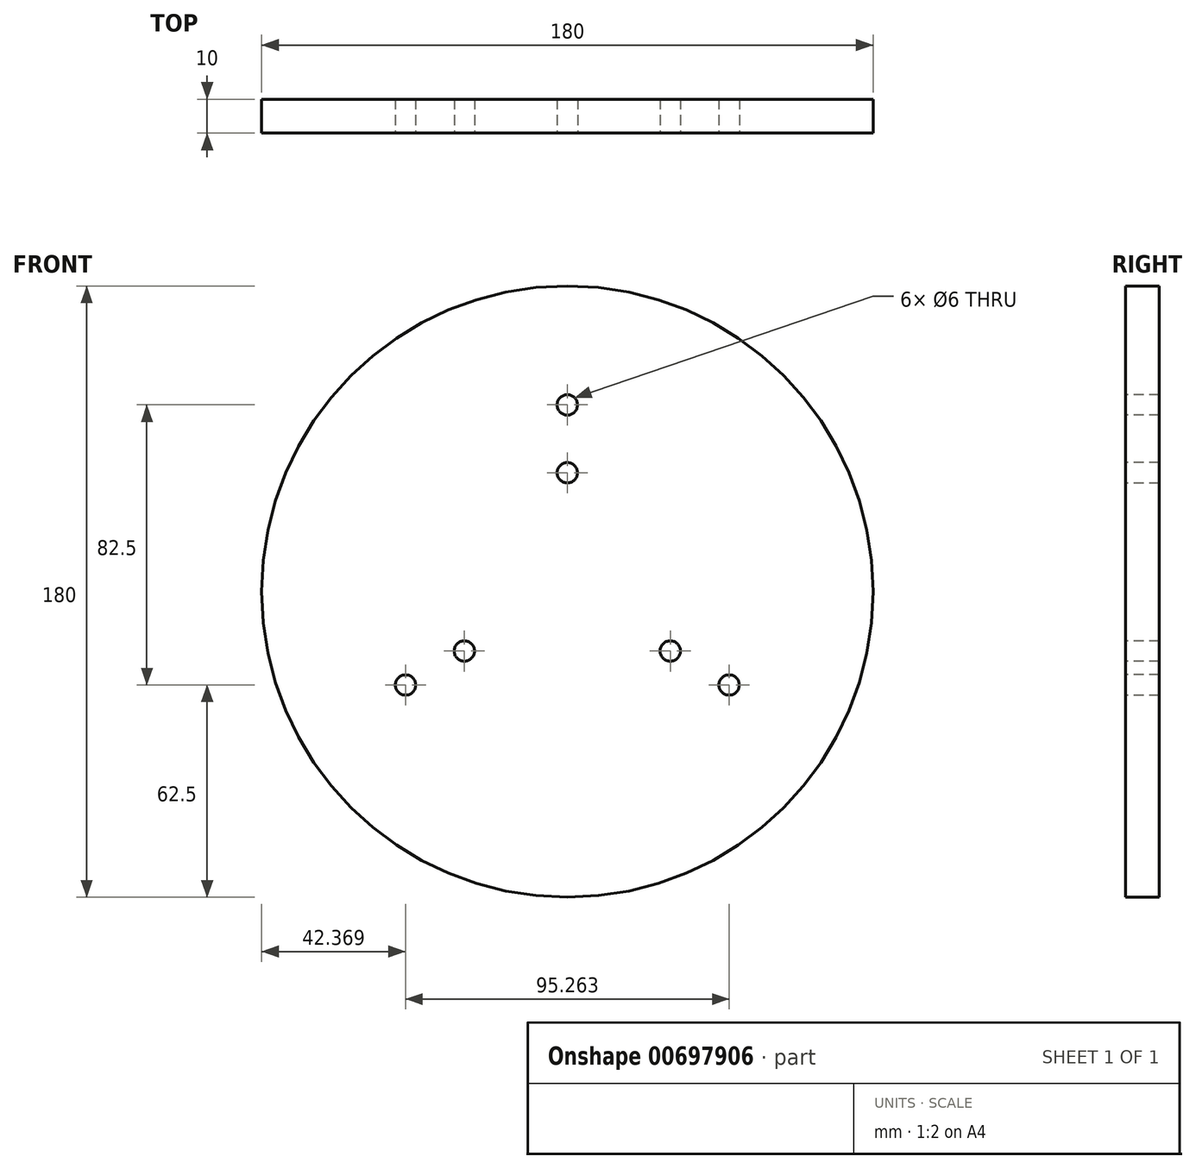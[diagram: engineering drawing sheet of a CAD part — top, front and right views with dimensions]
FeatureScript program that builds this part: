
annotation { "Feature Type Name" : "Feature", "Feature Type Description" : "" }
export const myFeature = defineFeature(function(context is Context, id is Id, definition is map)
    precondition{}
    {
        {
            var Q0;
            Q0=qCreatedBy(makeId("Front.planeOp"),FACE);
            var sketch = newSketch(context, id + "F0", { "sketchPlane" : qUnion([Q0])});
            skLineSegment(sketch, "E0.bottom", {"start": v(90, -90) * mm, "end": v(-90, -90) * mm});
            skLineSegment(sketch, "E0.top", {"start": v(90, 90) * mm, "end": v(-90, 90) * mm});
            skLineSegment(sketch, "E0.left", {"start": v(90, -90) * mm, "end": v(90, 90) * mm});
            skLineSegment(sketch, "E0.right", {"start": v(-90, -90) * mm, "end": v(-90, 90) * mm});
            skPoint(sketch, "E0.middle", {"position": v(0, 0) * mm});
            skSolve(sketch);
        }
        {
            var Q0;
            Q0=qSketchRegion(id+"F0",true);
            extrude(context, id + "F1", {"entities" : qUnion([Q0]), "oppositeDirection" : true, "depth" : 10 * mm, "offsetDistance" : 25 * mm});
        }
        {
            var Q0;
            Q0=makeQuery(id+"F0.imprint","IMPRINT",FACE,{"disambiguationData":[TD([[makeQuery(id+"F0.imprint","IMPRINT",EDGE,{"derivedFrom":sQuery(id+"F0.wireOp",EDGE,"E0.bottom")}),-1.0]])]});
            var sketch = newSketch(context, id + "F2", { "sketchPlane" : qUnion([Q0])});
            skPoint(sketch, "E1.middle", {"position": v(0, 0) * mm});
            skLineSegment(sketch, "E2", {"start": v(0, 90) * mm, "end": v(0, 0) * mm, "construction": true});
            skCircle(sketch, "E3", {"center": v(0, 55) * mm, "radius": 3 * mm});
            skCircle(sketch, "E4", {"center": v(0, 35) * mm, "radius": 3 * mm});
            skLineSegment(sketch, "E5.1.0", {"start": v(-77.94, -45) * mm, "end": v(0, 0) * mm, "construction": true});
            skCircle(sketch, "E5.1.1", {"center": v(-30.31, -17.5) * mm, "radius": 3 * mm});
            skCircle(sketch, "E5.1.2", {"center": v(-47.63, -27.5) * mm, "radius": 3 * mm});
            skLineSegment(sketch, "E5.2.0", {"start": v(77.94, -45) * mm, "end": v(0, 0) * mm, "construction": true});
            skCircle(sketch, "E5.2.1", {"center": v(30.31, -17.5) * mm, "radius": 3 * mm});
            skCircle(sketch, "E5.2.2", {"center": v(47.63, -27.5) * mm, "radius": 3 * mm});
            skSolve(sketch);
        }
        {
            var Q0;
            Q0=qSketchRegion(id+"F2",true);
            extrude(context, id + "F3", {"entities" : qUnion([Q0]), "operationType" : NewBodyOperationType.REMOVE, "endBound" : BoundingType.THROUGH_ALL, "oppositeDirection" : true, "depth" : 1 * mm, "offsetDistance" : 25 * mm});
        }
        {
            var Q0;
            Q0=makeQuery(id+"F0.imprint","IMPRINT",FACE,{"disambiguationData":[TD([[makeQuery(id+"F0.imprint","IMPRINT",EDGE,{"derivedFrom":sQuery(id+"F0.wireOp",EDGE,"E0.bottom")}),-1.0]])]});
            var sketch = newSketch(context, id + "F4", { "sketchPlane" : qUnion([Q0])});
            skCircle(sketch, "E6", {"center": v(0, 0) * mm, "radius": 90 * mm});
            skSolve(sketch);
        }
        {
            var Q0;
            {var subQ0=sQuery(id+"F4.wireOp",EDGE,"E6");var subQ1=makeQuery(id+"F0.imprint","IMPRINT",EDGE,{"derivedFrom":sQuery(id+"F0.wireOp",EDGE,"E0.top")});var subQ2=makeQuery(id+"F4.imprint","INTERSECT",VERTEX,{"derivedFrom":[subQ1,subQ0]});Q0=makeQuery(id+"F4.imprint","IMPRINT",FACE,{"disambiguationData":[TD([[makeQuery(id+"F4.imprint","IMPRINT",EDGE,{"disambiguationData":[TD([[subQ2,-1.0]])],"derivedFrom":subQ0}),-1.0]])]});}
            var Q1;
            {var subQ0=sQuery(id+"F4.wireOp",EDGE,"E6");var subQ1=makeQuery(id+"F0.imprint","IMPRINT",EDGE,{"derivedFrom":sQuery(id+"F0.wireOp",EDGE,"E0.top")});var subQ2=makeQuery(id+"F4.imprint","INTERSECT",VERTEX,{"derivedFrom":[subQ1,subQ0]});Q1=makeQuery(id+"F4.imprint","IMPRINT",FACE,{"disambiguationData":[TD([[makeQuery(id+"F4.imprint","IMPRINT",EDGE,{"disambiguationData":[TD([[subQ2,1.0]])],"derivedFrom":subQ0}),-1.0]])]});}
            var Q2;
            {var subQ0=sQuery(id+"F4.wireOp",EDGE,"E6");var subQ1=makeQuery(id+"F0.imprint","IMPRINT",EDGE,{"derivedFrom":sQuery(id+"F0.wireOp",EDGE,"E0.left")});var subQ2=makeQuery(id+"F4.imprint","INTERSECT",VERTEX,{"derivedFrom":[subQ1,subQ0]});Q2=makeQuery(id+"F4.imprint","IMPRINT",FACE,{"disambiguationData":[TD([[makeQuery(id+"F4.imprint","IMPRINT",EDGE,{"disambiguationData":[TD([[subQ2,1.0]])],"derivedFrom":subQ0}),-1.0]])]});}
            var Q3;
            {var subQ0=sQuery(id+"F4.wireOp",EDGE,"E6");var subQ1=makeQuery(id+"F0.imprint","IMPRINT",EDGE,{"derivedFrom":sQuery(id+"F0.wireOp",EDGE,"E0.right")});var subQ2=makeQuery(id+"F4.imprint","INTERSECT",VERTEX,{"derivedFrom":[subQ1,subQ0]});Q3=makeQuery(id+"F4.imprint","IMPRINT",FACE,{"disambiguationData":[TD([[makeQuery(id+"F4.imprint","IMPRINT",EDGE,{"disambiguationData":[TD([[subQ2,-1.0]])],"derivedFrom":subQ0}),-1.0]])]});}
            extrude(context, id + "F5", {"entities" : qUnion([Q0, Q1, Q2, Q3]), "operationType" : NewBodyOperationType.REMOVE, "endBound" : BoundingType.THROUGH_ALL, "oppositeDirection" : true, "depth" : 25 * mm, "offsetDistance" : 25 * mm});
        }
    });
